# Revit family: Hager-Orion_Plus-IP65-D300-Cl.II-Poly_double_encl-630A-CH-fr
name_source: partatom
category: Electrical Equipment
units: mm (PartAtom-declared; Revit-internal decimal feet)

## family parameters
Cut with Voids When Loaded = No
Host = Face
Panel Configuration = Two Columns, Circuits Across
Part Type = Panelboard
Room Calculation Point = No
Round Connector Dimension = Use Diameter
Shared = No

## types (6) — shared parameters
EF000003 - mode de pose = EV000384 - saillie
EF000007 - couleur = EV000270 - gris
EF000049 - profondeur = 300 mm  [stored 0.984252 ft]
EF000116 - numéro RAL = 7035
EF000266 - nombre de rangées = 3
EF001131 - profondeur intérieure = 300 mm  [stored 0.984252 ft]
EF001596 - matériau du boîtier/corps = EV000139 - plastique
EF001613 - maintien de fonction = EV000494 - sans
EF004464 - type de porte = EV002646 - unique
EF005474 - indice de protection (IP) = EV006421 - IP65
EF006306 - avec serrure = Yes
EF007800 - adapté à un parafoudre = No
EF008873 - courant nominal (In) = 630 A
EF009170 - épaisseur de matériau du boîtier = 2 mm  [stored 0.00656168 ft]
EF009171 - épaisseur de matériau de la porte/du couvercle = 2 mm  [stored 0.00656168 ft]
EF015940 - couvercle avec décharge de pression = No
HG000003 - Gamme = Orion Plus
HG000006 - Encastré = No
HG000010 - Portes asymétriques = No
HG000023 - Armoire double section = Yes
HG000024 - Hauteur de la section basse = 800 mm  [stored 2.62467 ft]
HG000026 - Installation au sol = No
HG000027 - Hauteur du socle = 70 mm  [stored 0.229659 ft]
Manufacturer = Hager
Type Comments = Orion Plus
zero-valued in all types: Default Elevation, EF000218 - profondeur d'encastrement, EF000437 - nombre d'entrées de conduit, EF002950 - largeur en nombre de modules, EF009554 - nombre d'ouvertures pour plaques à bride

## per-type parameters (varying)
| type | EF000008 - largeur | EF000040 - hauteur | EF000118 - avec cadre/support de montage | EF000339 - type de capot | EF001088 - possibilité de montage en saillie | EF003532 - convient pour utilisation à l’extérieur | EF004293 - indice de protection contre les chocs (IK) | EF004427 - nombre de modules | EF006244 - couvercle/porte transparent(e) | EF009212 - finition du couvercle | HG000002 - avec porte | HG000004 - Référence fabricant | HG000009 - Porte à double battant |
| saillie IP65 L1100 H1150 P300  - FL360B | 1100 mm | 1150 mm | No | EV004216 - porte | Yes | Yes | EV008784 - IK10 | 138 | Yes | EV009916 - avec échancrure | Yes | FL360B | Yes |
| saillie IP65 L1100 H1450 P300  - FL362B | 1100 mm | 1450 mm | No | EV004216 - porte | Yes | Yes | EV008784 - IK10 | 138 | Yes | EV009916 - avec échancrure | Yes | FL362B | Yes |
| saillie IP65 L600 H1150 P300  - FL340B | 600 mm | 1150 mm | No | EV004216 - porte | Yes | Yes | EV008784 - IK10 | 69 | Yes | EV009916 - avec échancrure | Yes | FL340B | No |
| saillie IP65 L600 H1450 P300  - FL342B | 600 mm | 1450 mm | No | EV004216 - porte | Yes | Yes | EV008784 - IK10 | 69 | Yes | EV009916 - avec échancrure | No | FL342B | No |
| saillie IP65 L850 H1150 P300  - FL350B | 850 mm  [stored 2.78871 ft] | 1150 mm | No | EV004216 - porte | Yes | Yes | EV008784 - IK10 | 111 | Yes | EV009916 - avec échancrure | Yes | FL350B | No |
| saillie IP65 L850 H1450 P300  - FL352B | 850 mm  [stored 2.78871 ft] | 1450 mm | Yes | EV001012 - couvercle | No | No | EV006814 - IK08 | 111 | No | EV000116 - fermé | Yes | FL352B | No |

note: [stored X ft] marks values corroborated as IEEE doubles in the binary element streams (Revit-internal decimal feet)

## geometry (parser evidence)
native form markers: Sweep x10
no freeform markers — native parametric forms only
